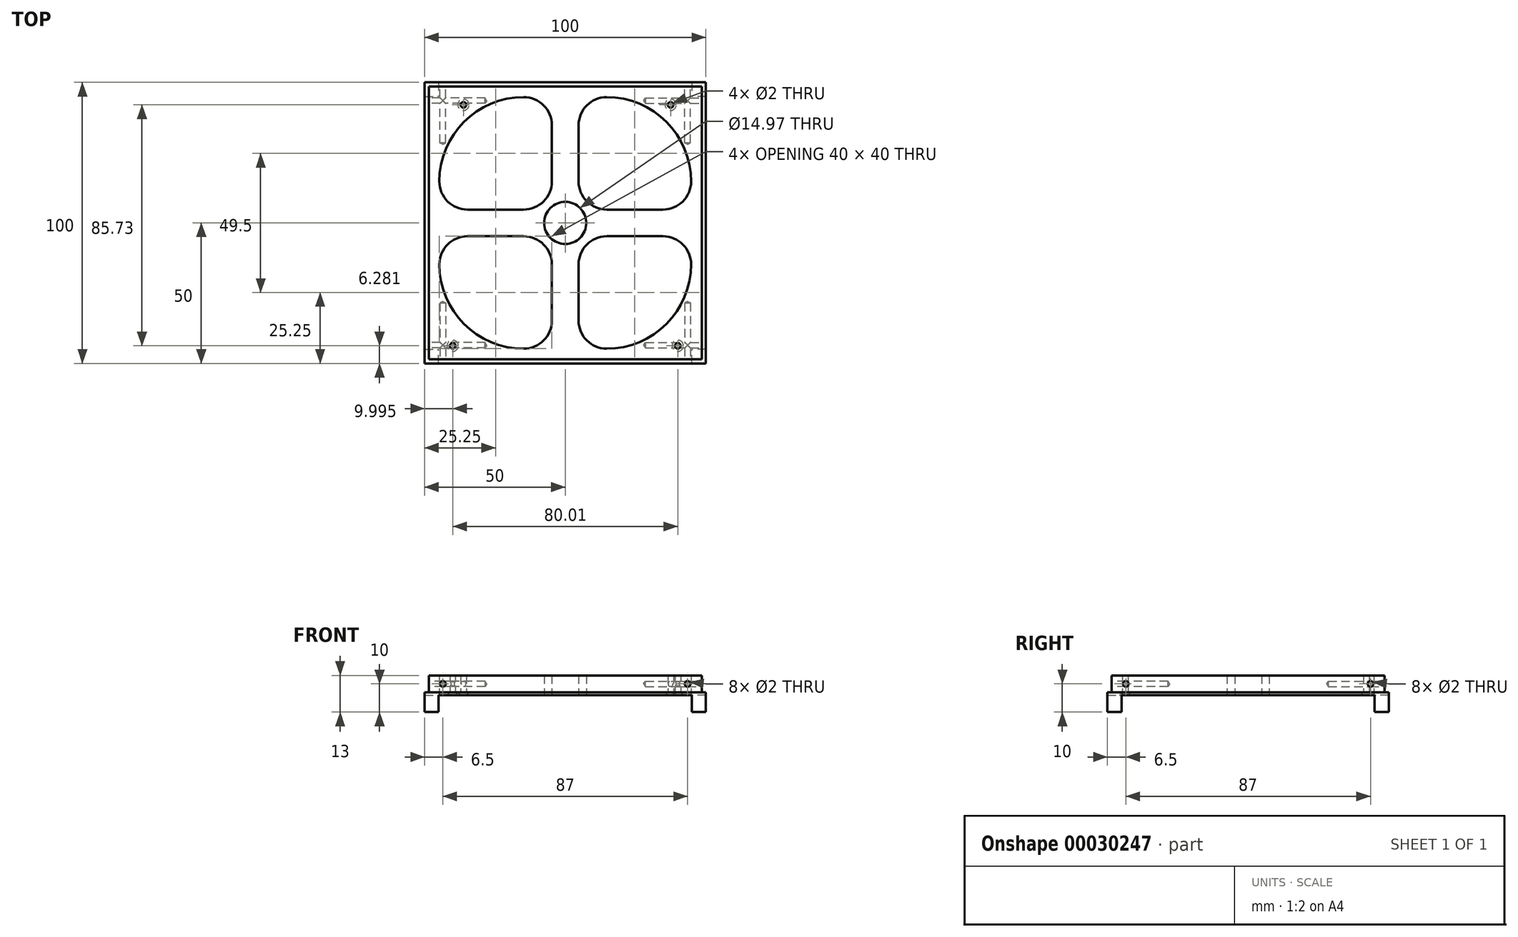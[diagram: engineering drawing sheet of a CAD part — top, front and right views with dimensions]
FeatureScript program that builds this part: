
annotation { "Feature Type Name" : "Feature", "Feature Type Description" : "" }
export const myFeature = defineFeature(function(context is Context, id is Id, definition is map)
    precondition{}
    {
        {
            var Q0;
            Q0=qCreatedBy(makeId("Top.planeOp"),FACE);
            var sketch = newSketch(context, id + "F0", { "sketchPlane" : qUnion([Q0])});
            skLineSegment(sketch, "E0.rect.bottom", {"start": v(-50, 50) * mm, "end": v(50, 50) * mm});
            skLineSegment(sketch, "E0.rect.top", {"start": v(-50, -50) * mm, "end": v(50, -50) * mm});
            skLineSegment(sketch, "E0.rect.left", {"start": v(-50, 50) * mm, "end": v(-50, -50) * mm});
            skLineSegment(sketch, "E0.rect.right", {"start": v(50, 50) * mm, "end": v(50, -50) * mm});
            skPoint(sketch, "E0.rect.middle", {"position": v(0, 0) * mm});
            skLineSegment(sketch, "E1.rect.bottom", {"start": v(-48.5, 48.5) * mm, "end": v(48.5, 48.5) * mm});
            skLineSegment(sketch, "E1.rect.top", {"start": v(-48.5, -48.5) * mm, "end": v(48.5, -48.5) * mm});
            skLineSegment(sketch, "E1.rect.left", {"start": v(-48.5, 48.5) * mm, "end": v(-48.5, -48.5) * mm});
            skLineSegment(sketch, "E1.rect.right", {"start": v(48.5, 48.5) * mm, "end": v(48.5, -48.5) * mm});
            skLineSegment(sketch, "E2.rect.bottom", {"start": v(-14.75, 4.75) * mm, "end": v(-34.75, 4.75) * mm});
            skLineSegment(sketch, "E2.rect.top", {"start": v(-14.75, 44.75) * mm, "end": v(-14.75, 44.75) * mm});
            skLineSegment(sketch, "E2.rect.left", {"start": v(-4.75, 14.75) * mm, "end": v(-4.75, 34.75) * mm});
            skLineSegment(sketch, "E2.rect.right", {"start": v(-44.75, 14.75) * mm, "end": v(-44.75, 14.75) * mm});
            skPoint(sketch, "E2.rect.middle", {"position": v(-24.75, 24.75) * mm});
            skPoint(sketch, "E3.visualSharp", {"position": v(-44.75, 44.75) * mm});
            skArc(sketch, "E3.filletArc", {"start": v(-14.75, 44.75) * mm, "mid": v(-35.96, 35.96) * mm, "end": v(-44.75, 14.75) * mm});
            skPoint(sketch, "E4.visualSharp", {"position": v(-4.75, 44.75) * mm});
            skArc(sketch, "E4.filletArc", {"start": v(-4.75, 34.75) * mm, "mid": v(-7.68, 41.82) * mm, "end": v(-14.75, 44.75) * mm});
            skPoint(sketch, "E5.visualSharp", {"position": v(-4.75, 4.75) * mm});
            skArc(sketch, "E5.filletArc", {"start": v(-14.75, 4.75) * mm, "mid": v(-7.68, 7.68) * mm, "end": v(-4.75, 14.75) * mm});
            skPoint(sketch, "E6.visualSharp", {"position": v(-44.75, 4.75) * mm});
            skArc(sketch, "E6.filletArc", {"start": v(-44.75, 14.75) * mm, "mid": v(-41.82, 7.68) * mm, "end": v(-34.75, 4.75) * mm});
            skLineSegment(sketch, "E7.MirrorCS", {"start": v(4.75, 14.75) * mm, "end": v(4.75, 34.75) * mm});
            skArc(sketch, "E8.MirrorCS", {"start": v(4.75, 34.75) * mm, "mid": v(7.68, 41.82) * mm, "end": v(14.75, 44.75) * mm});
            skLineSegment(sketch, "E9.MirrorCS", {"start": v(14.75, 44.75) * mm, "end": v(14.75, 44.75) * mm});
            skArc(sketch, "E10.MirrorCS", {"start": v(14.75, 44.75) * mm, "mid": v(35.96, 35.96) * mm, "end": v(44.75, 14.75) * mm});
            skLineSegment(sketch, "E11.MirrorCS", {"start": v(44.75, 14.75) * mm, "end": v(44.75, 14.75) * mm});
            skArc(sketch, "E12.MirrorCS", {"start": v(44.75, 14.75) * mm, "mid": v(41.82, 7.68) * mm, "end": v(34.75, 4.75) * mm});
            skLineSegment(sketch, "E13.MirrorCS", {"start": v(14.75, 4.75) * mm, "end": v(34.75, 4.75) * mm});
            skArc(sketch, "E14.MirrorCS", {"start": v(14.75, 4.75) * mm, "mid": v(7.68, 7.68) * mm, "end": v(4.75, 14.75) * mm});
            skPoint(sketch, "E15.MirrorP", {"position": v(24.75, 24.75) * mm});
            skArc(sketch, "E16.MirrorCS", {"start": v(14.75, -4.75) * mm, "mid": v(7.68, -7.68) * mm, "end": v(4.75, -14.75) * mm});
            skLineSegment(sketch, "E17.MirrorCS", {"start": v(4.75, -14.75) * mm, "end": v(4.75, -34.75) * mm});
            skArc(sketch, "E18.MirrorCS", {"start": v(4.75, -34.75) * mm, "mid": v(7.68, -41.82) * mm, "end": v(14.75, -44.75) * mm});
            skLineSegment(sketch, "E19.MirrorCS", {"start": v(14.75, -44.75) * mm, "end": v(14.75, -44.75) * mm});
            skArc(sketch, "E20.MirrorCS", {"start": v(14.75, -44.75) * mm, "mid": v(35.96, -35.96) * mm, "end": v(44.75, -14.75) * mm});
            skLineSegment(sketch, "E21.MirrorCS", {"start": v(44.75, -14.75) * mm, "end": v(44.75, -14.75) * mm});
            skArc(sketch, "E22.MirrorCS", {"start": v(44.75, -14.75) * mm, "mid": v(41.82, -7.68) * mm, "end": v(34.75, -4.75) * mm});
            skLineSegment(sketch, "E23.MirrorCS", {"start": v(14.75, -4.75) * mm, "end": v(34.75, -4.75) * mm});
            skPoint(sketch, "E24.MirrorP", {"position": v(24.75, -24.75) * mm});
            skLineSegment(sketch, "E25.MirrorCS", {"start": v(-4.75, -14.75) * mm, "end": v(-4.75, -34.75) * mm});
            skArc(sketch, "E26.MirrorCS", {"start": v(-14.75, -4.75) * mm, "mid": v(-7.68, -7.68) * mm, "end": v(-4.75, -14.75) * mm});
            skLineSegment(sketch, "E27.MirrorCS", {"start": v(-14.75, -4.75) * mm, "end": v(-34.75, -4.75) * mm});
            skArc(sketch, "E28.MirrorCS", {"start": v(-44.75, -14.75) * mm, "mid": v(-41.82, -7.68) * mm, "end": v(-34.75, -4.75) * mm});
            skLineSegment(sketch, "E29.MirrorCS", {"start": v(-44.75, -14.75) * mm, "end": v(-44.75, -14.75) * mm});
            skArc(sketch, "E30.MirrorCS", {"start": v(-14.75, -44.75) * mm, "mid": v(-35.96, -35.96) * mm, "end": v(-44.75, -14.75) * mm});
            skLineSegment(sketch, "E31.MirrorCS", {"start": v(-14.75, -44.75) * mm, "end": v(-14.75, -44.75) * mm});
            skArc(sketch, "E32.MirrorCS", {"start": v(-4.75, -34.75) * mm, "mid": v(-7.68, -41.82) * mm, "end": v(-14.75, -44.75) * mm});
            skPoint(sketch, "E33.MirrorP", {"position": v(-24.75, -24.75) * mm});
            skCircle(sketch, "E34", {"center": v(0, 0) * mm, "radius": 7.48 * mm});
            skPoint(sketch, "E35", {"position": v(-40, -42.87) * mm});
            skPoint(sketch, "E36", {"position": v(-48.5, 0) * mm});
            skPoint(sketch, "E37", {"position": v(48.5, 0) * mm});
            skLineSegment(sketch, "E38", {"start": v(-48.5, 0) * mm, "end": v(48.5, 0) * mm});
            skPoint(sketch, "E39.MirrorP", {"position": v(40, -42.87) * mm});
            skPoint(sketch, "E40", {"position": v(-36.2, 42.87) * mm});
            skPoint(sketch, "E41", {"position": v(37.47, 42.87) * mm});
            skSolve(sketch);
        }
        {
            var Q0;
            Q0=makeQuery(id+"F0.imprint","IMPRINT",FACE,{"disambiguationData":[TD([[makeQuery(id+"F0.imprint","IMPRINT",EDGE,{"derivedFrom":sQuery(id+"F0.wireOp",EDGE,"E1.rect.bottom")}),-1.0]])]});
            var Q1;
            {var subQ4=sQuery(id+"F0.wireOp",EDGE,"E1.rect.top");Q1=makeQuery(id+"F0.imprint","IMPRINT",FACE,{"disambiguationData":[TD([[makeQuery(id+"F0.imprint","IMPRINT",EDGE,{"derivedFrom":subQ4}),1.0]])]});}
            extrude(context, id + "F1", {"entities" : qUnion([Q0, Q1]), "depth" : 6 * mm});
        }
        {
            var Q0;
            Q0 = qSketchRegion(id + "F0", true);
            var Q1;
            Q1=makeQuery(id+"F1.opExtrude","CAP_FACE",FACE,{"disambiguationData":[OSD([sQuery(id+"F0.wireOp",EDGE,"E1.rect.bottom"),sQuery(id+"F0.wireOp",EDGE,"E1.rect.top"),sQuery(id+"F0.wireOp",EDGE,"E1.rect.left"),sQuery(id+"F0.wireOp",EDGE,"E1.rect.right"),sQuery(id+"F0.wireOp",EDGE,"E2.rect.bottom"),sQuery(id+"F0.wireOp",EDGE,"E2.rect.top"),sQuery(id+"F0.wireOp",EDGE,"E2.rect.left"),sQuery(id+"F0.wireOp",EDGE,"E2.rect.right"),sQuery(id+"F0.wireOp",EDGE,"d764ca65-7f6a-4e13-98eb-a7907a3d072d0.MirrorCS"),sQuery(id+"F0.wireOp",EDGE,"4e8c5bec-c53d-4312-8259-349e49f543fe0.MirrorCS"),sQuery(id+"F0.wireOp",EDGE,"d6a0bf7c-e4bc-484e-b3d5-183d898144500.MirrorCS"),sQuery(id+"F0.wireOp",EDGE,"45a758ec-378c-46c5-b086-a70cc1cacffd0.MirrorCS"),sQuery(id+"F0.wireOp",EDGE,"a64d5360-d78c-41ef-9f44-8c8436a09bba0.MirrorCS"),sQuery(id+"F0.wireOp",EDGE,"c998a958-b69a-464e-a296-dd7f6d349ec80.MirrorCS"),sQuery(id+"F0.wireOp",EDGE,"a4bf1b2a-a2f4-4ab3-9d73-85797b196d270.MirrorCS"),sQuery(id+"F0.wireOp",EDGE,"ecd2f3fb-4ea3-4913-80f4-94ebebe2d04e0.MirrorCS"),sQuery(id+"F0.wireOp",EDGE,"085a2cb5-2e3f-4cc3-a5b9-01c6e75669f10.MirrorCS"),sQuery(id+"F0.wireOp",EDGE,"73d67a52-dadc-4bd6-8141-d25047cb753b0.MirrorCS"),sQuery(id+"F0.wireOp",EDGE,"8f6832c0-858d-4205-8574-29f35786d1620.MirrorCS"),sQuery(id+"F0.wireOp",EDGE,"ecc9a695-4792-4055-9804-abf58933c5b20.MirrorCS")])],"isStart":false});
            extrude(context, id + "F2", {"entities" : qUnion([Q0, Q1]), "operationType" : NewBodyOperationType.ADD, "depth" : 1 * mm});
        }
        {
            var Q0;
            {var subQ0=sQuery(id+"F0.wireOp",EDGE,"E1.rect.bottom");Q0=makeQuery(id+"F2.boolean.opBoolean","MERGE",FACE,{"derivedFrom":[makeQuery(id+"F1.opExtrude","SWEPT_FACE",FACE,{"disambiguationData":[OSD([subQ0])]}),makeQuery(id+"F2.opExtrude","SWEPT_FACE",FACE,{"disambiguationData":[OSD([subQ0]),TDD([makeQuery(id+"F1.opExtrude","CAP_EDGE",EDGE,{"disambiguationData":[OSD([subQ0])],"isStart":false})])]})]});}
            var sketch = newSketch(context, id + "F3", { "sketchPlane" : qUnion([Q0])});
            skPoint(sketch, "E42", {"position": v(-43.5, 4) * mm});
            skPoint(sketch, "E43.MirrorP", {"position": v(43.5, 4) * mm});
            skSolve(sketch);
        }
        {
            var Q0;
            Q0=sQuery(id+"F3.wireOp",VERTEX,"E42");
            var Q1;
            Q1=sQuery(id+"F3.wireOp",VERTEX,"E43.MirrorP");
            var Q2;
            Q2=makeQuery(id+"F1.opExtrude","SWEPT_BODY",BODY,{"disambiguationData":[OSD([sQuery(id+"F0.wireOp",EDGE,"E1.rect.bottom"),sQuery(id+"F0.wireOp",EDGE,"E1.rect.top"),sQuery(id+"F0.wireOp",EDGE,"E1.rect.left"),sQuery(id+"F0.wireOp",EDGE,"E1.rect.right"),sQuery(id+"F0.wireOp",EDGE,"E2.rect.bottom"),sQuery(id+"F0.wireOp",EDGE,"E2.rect.top"),sQuery(id+"F0.wireOp",EDGE,"E2.rect.left"),sQuery(id+"F0.wireOp",EDGE,"E2.rect.right"),sQuery(id+"F0.wireOp",EDGE,"E3.filletArc"),sQuery(id+"F0.wireOp",EDGE,"E4.filletArc"),sQuery(id+"F0.wireOp",EDGE,"E5.filletArc"),sQuery(id+"F0.wireOp",EDGE,"E6.filletArc"),sQuery(id+"F0.wireOp",EDGE,"E7.MirrorCS"),sQuery(id+"F0.wireOp",EDGE,"E8.MirrorCS"),sQuery(id+"F0.wireOp",EDGE,"E9.MirrorCS"),sQuery(id+"F0.wireOp",EDGE,"E10.MirrorCS"),sQuery(id+"F0.wireOp",EDGE,"E11.MirrorCS"),sQuery(id+"F0.wireOp",EDGE,"E12.MirrorCS"),sQuery(id+"F0.wireOp",EDGE,"E13.MirrorCS"),sQuery(id+"F0.wireOp",EDGE,"E14.MirrorCS"),sQuery(id+"F0.wireOp",EDGE,"E16.MirrorCS"),sQuery(id+"F0.wireOp",EDGE,"E17.MirrorCS"),sQuery(id+"F0.wireOp",EDGE,"E18.MirrorCS"),sQuery(id+"F0.wireOp",EDGE,"E19.MirrorCS"),sQuery(id+"F0.wireOp",EDGE,"E20.MirrorCS"),sQuery(id+"F0.wireOp",EDGE,"E21.MirrorCS"),sQuery(id+"F0.wireOp",EDGE,"E22.MirrorCS"),sQuery(id+"F0.wireOp",EDGE,"E23.MirrorCS"),sQuery(id+"F0.wireOp",EDGE,"E25.MirrorCS"),sQuery(id+"F0.wireOp",EDGE,"E26.MirrorCS"),sQuery(id+"F0.wireOp",EDGE,"E27.MirrorCS"),sQuery(id+"F0.wireOp",EDGE,"E28.MirrorCS"),sQuery(id+"F0.wireOp",EDGE,"E29.MirrorCS"),sQuery(id+"F0.wireOp",EDGE,"E30.MirrorCS"),sQuery(id+"F0.wireOp",EDGE,"E31.MirrorCS"),sQuery(id+"F0.wireOp",EDGE,"E32.MirrorCS")])]});
            hole(context, id + "F4", {"style" : HoleStyle.SIMPLE, "holeDiameter" : 2 * mm, "endStyle" : HoleEndStyle.BLIND, "holeDepth" : 20 * mm, "locations" : qUnion([Q0, Q1]), "scope" : qUnion([Q2])});
        }
        {
            var Q0;
            {var subQ0=sQuery(id+"F0.wireOp",EDGE,"E1.rect.left");Q0=makeQuery(id+"F2.boolean.opBoolean","MERGE",FACE,{"derivedFrom":[makeQuery(id+"F1.opExtrude","SWEPT_FACE",FACE,{"disambiguationData":[OSD([subQ0])]}),makeQuery(id+"F2.opExtrude","SWEPT_FACE",FACE,{"disambiguationData":[OSD([subQ0]),TDD([makeQuery(id+"F1.opExtrude","CAP_EDGE",EDGE,{"disambiguationData":[OSD([subQ0])],"isStart":false})])]})]});}
            var sketch = newSketch(context, id + "F5", { "sketchPlane" : qUnion([Q0])});
            skPoint(sketch, "E44", {"position": v(-43.5, 4) * mm});
            skPoint(sketch, "E45.MirrorP", {"position": v(43.5, 4) * mm});
            skSolve(sketch);
        }
        {
            var Q0;
            Q0=sQuery(id+"F5.wireOp",VERTEX,"E44");
            var Q1;
            Q1=sQuery(id+"F5.wireOp",VERTEX,"E45.MirrorP");
            var Q2;
            Q2=makeQuery(id+"F1.opExtrude","SWEPT_BODY",BODY,{"disambiguationData":[OSD([sQuery(id+"F0.wireOp",EDGE,"E1.rect.bottom"),sQuery(id+"F0.wireOp",EDGE,"E1.rect.top"),sQuery(id+"F0.wireOp",EDGE,"E1.rect.left"),sQuery(id+"F0.wireOp",EDGE,"E1.rect.right"),sQuery(id+"F0.wireOp",EDGE,"E2.rect.bottom"),sQuery(id+"F0.wireOp",EDGE,"E2.rect.top"),sQuery(id+"F0.wireOp",EDGE,"E2.rect.left"),sQuery(id+"F0.wireOp",EDGE,"E2.rect.right"),sQuery(id+"F0.wireOp",EDGE,"E3.filletArc"),sQuery(id+"F0.wireOp",EDGE,"E4.filletArc"),sQuery(id+"F0.wireOp",EDGE,"E5.filletArc"),sQuery(id+"F0.wireOp",EDGE,"E6.filletArc"),sQuery(id+"F0.wireOp",EDGE,"E7.MirrorCS"),sQuery(id+"F0.wireOp",EDGE,"E8.MirrorCS"),sQuery(id+"F0.wireOp",EDGE,"E9.MirrorCS"),sQuery(id+"F0.wireOp",EDGE,"E10.MirrorCS"),sQuery(id+"F0.wireOp",EDGE,"E11.MirrorCS"),sQuery(id+"F0.wireOp",EDGE,"E12.MirrorCS"),sQuery(id+"F0.wireOp",EDGE,"E13.MirrorCS"),sQuery(id+"F0.wireOp",EDGE,"E14.MirrorCS"),sQuery(id+"F0.wireOp",EDGE,"E16.MirrorCS"),sQuery(id+"F0.wireOp",EDGE,"E17.MirrorCS"),sQuery(id+"F0.wireOp",EDGE,"E18.MirrorCS"),sQuery(id+"F0.wireOp",EDGE,"E19.MirrorCS"),sQuery(id+"F0.wireOp",EDGE,"E20.MirrorCS"),sQuery(id+"F0.wireOp",EDGE,"E21.MirrorCS"),sQuery(id+"F0.wireOp",EDGE,"E22.MirrorCS"),sQuery(id+"F0.wireOp",EDGE,"E23.MirrorCS"),sQuery(id+"F0.wireOp",EDGE,"E25.MirrorCS"),sQuery(id+"F0.wireOp",EDGE,"E26.MirrorCS"),sQuery(id+"F0.wireOp",EDGE,"E27.MirrorCS"),sQuery(id+"F0.wireOp",EDGE,"E28.MirrorCS"),sQuery(id+"F0.wireOp",EDGE,"E29.MirrorCS"),sQuery(id+"F0.wireOp",EDGE,"E30.MirrorCS"),sQuery(id+"F0.wireOp",EDGE,"E31.MirrorCS"),sQuery(id+"F0.wireOp",EDGE,"E32.MirrorCS")])]});
            hole(context, id + "F6", {"style" : HoleStyle.SIMPLE, "holeDiameter" : 2 * mm, "endStyle" : HoleEndStyle.BLIND, "holeDepth" : 20 * mm, "locations" : qUnion([Q0, Q1]), "scope" : qUnion([Q2])});
        }
        {
            var Q0;
            {var subQ0=sQuery(id+"F0.wireOp",EDGE,"E1.rect.top");Q0=makeQuery(id+"F2.boolean.opBoolean","MERGE",FACE,{"derivedFrom":[makeQuery(id+"F1.opExtrude","SWEPT_FACE",FACE,{"disambiguationData":[OSD([subQ0])]}),makeQuery(id+"F2.opExtrude","SWEPT_FACE",FACE,{"disambiguationData":[OSD([subQ0]),TDD([makeQuery(id+"F1.opExtrude","CAP_EDGE",EDGE,{"disambiguationData":[OSD([subQ0])],"isStart":false})])]})]});}
            var sketch = newSketch(context, id + "F7", { "sketchPlane" : qUnion([Q0])});
            skPoint(sketch, "E46", {"position": v(-43.5, 4) * mm});
            skPoint(sketch, "E47.MirrorP", {"position": v(43.5, 4) * mm});
            skSolve(sketch);
        }
        {
            var Q0;
            Q0=sQuery(id+"F7.wireOp",VERTEX,"E46");
            var Q1;
            Q1=sQuery(id+"F7.wireOp",VERTEX,"E47.MirrorP");
            var Q2;
            Q2=makeQuery(id+"F1.opExtrude","SWEPT_BODY",BODY,{"disambiguationData":[OSD([sQuery(id+"F0.wireOp",EDGE,"E1.rect.bottom"),sQuery(id+"F0.wireOp",EDGE,"E1.rect.top"),sQuery(id+"F0.wireOp",EDGE,"E1.rect.left"),sQuery(id+"F0.wireOp",EDGE,"E1.rect.right"),sQuery(id+"F0.wireOp",EDGE,"E2.rect.bottom"),sQuery(id+"F0.wireOp",EDGE,"E2.rect.top"),sQuery(id+"F0.wireOp",EDGE,"E2.rect.left"),sQuery(id+"F0.wireOp",EDGE,"E2.rect.right"),sQuery(id+"F0.wireOp",EDGE,"E3.filletArc"),sQuery(id+"F0.wireOp",EDGE,"E4.filletArc"),sQuery(id+"F0.wireOp",EDGE,"E5.filletArc"),sQuery(id+"F0.wireOp",EDGE,"E6.filletArc"),sQuery(id+"F0.wireOp",EDGE,"E7.MirrorCS"),sQuery(id+"F0.wireOp",EDGE,"E8.MirrorCS"),sQuery(id+"F0.wireOp",EDGE,"E9.MirrorCS"),sQuery(id+"F0.wireOp",EDGE,"E10.MirrorCS"),sQuery(id+"F0.wireOp",EDGE,"E11.MirrorCS"),sQuery(id+"F0.wireOp",EDGE,"E12.MirrorCS"),sQuery(id+"F0.wireOp",EDGE,"E13.MirrorCS"),sQuery(id+"F0.wireOp",EDGE,"E14.MirrorCS"),sQuery(id+"F0.wireOp",EDGE,"E16.MirrorCS"),sQuery(id+"F0.wireOp",EDGE,"E17.MirrorCS"),sQuery(id+"F0.wireOp",EDGE,"E18.MirrorCS"),sQuery(id+"F0.wireOp",EDGE,"E19.MirrorCS"),sQuery(id+"F0.wireOp",EDGE,"E20.MirrorCS"),sQuery(id+"F0.wireOp",EDGE,"E21.MirrorCS"),sQuery(id+"F0.wireOp",EDGE,"E22.MirrorCS"),sQuery(id+"F0.wireOp",EDGE,"E23.MirrorCS"),sQuery(id+"F0.wireOp",EDGE,"E25.MirrorCS"),sQuery(id+"F0.wireOp",EDGE,"E26.MirrorCS"),sQuery(id+"F0.wireOp",EDGE,"E27.MirrorCS"),sQuery(id+"F0.wireOp",EDGE,"E28.MirrorCS"),sQuery(id+"F0.wireOp",EDGE,"E29.MirrorCS"),sQuery(id+"F0.wireOp",EDGE,"E30.MirrorCS"),sQuery(id+"F0.wireOp",EDGE,"E31.MirrorCS"),sQuery(id+"F0.wireOp",EDGE,"E32.MirrorCS")])]});
            hole(context, id + "F8", {"style" : HoleStyle.SIMPLE, "holeDiameter" : 2 * mm, "endStyle" : HoleEndStyle.BLIND, "holeDepth" : 20 * mm, "locations" : qUnion([Q0, Q1]), "scope" : qUnion([Q2])});
        }
        {
            var Q0;
            {var subQ0=sQuery(id+"F0.wireOp",EDGE,"E1.rect.right");Q0=makeQuery(id+"F2.boolean.opBoolean","MERGE",FACE,{"derivedFrom":[makeQuery(id+"F1.opExtrude","SWEPT_FACE",FACE,{"disambiguationData":[OSD([subQ0])]}),makeQuery(id+"F2.opExtrude","SWEPT_FACE",FACE,{"disambiguationData":[OSD([subQ0]),TDD([makeQuery(id+"F1.opExtrude","CAP_EDGE",EDGE,{"disambiguationData":[OSD([subQ0])],"isStart":false})])]})]});}
            var sketch = newSketch(context, id + "F9", { "sketchPlane" : qUnion([Q0])});
            skPoint(sketch, "E48", {"position": v(-43.5, 4) * mm});
            skPoint(sketch, "E49.MirrorP", {"position": v(43.5, 4) * mm});
            skSolve(sketch);
        }
        {
            var Q0;
            Q0=sQuery(id+"F9.wireOp",VERTEX,"E48");
            var Q1;
            Q1=sQuery(id+"F9.wireOp",VERTEX,"E49.MirrorP");
            var Q2;
            Q2=makeQuery(id+"F1.opExtrude","SWEPT_BODY",BODY,{"disambiguationData":[OSD([sQuery(id+"F0.wireOp",EDGE,"E1.rect.bottom"),sQuery(id+"F0.wireOp",EDGE,"E1.rect.top"),sQuery(id+"F0.wireOp",EDGE,"E1.rect.left"),sQuery(id+"F0.wireOp",EDGE,"E1.rect.right"),sQuery(id+"F0.wireOp",EDGE,"E2.rect.bottom"),sQuery(id+"F0.wireOp",EDGE,"E2.rect.top"),sQuery(id+"F0.wireOp",EDGE,"E2.rect.left"),sQuery(id+"F0.wireOp",EDGE,"E2.rect.right"),sQuery(id+"F0.wireOp",EDGE,"E3.filletArc"),sQuery(id+"F0.wireOp",EDGE,"E4.filletArc"),sQuery(id+"F0.wireOp",EDGE,"E5.filletArc"),sQuery(id+"F0.wireOp",EDGE,"E6.filletArc"),sQuery(id+"F0.wireOp",EDGE,"E7.MirrorCS"),sQuery(id+"F0.wireOp",EDGE,"E8.MirrorCS"),sQuery(id+"F0.wireOp",EDGE,"E9.MirrorCS"),sQuery(id+"F0.wireOp",EDGE,"E10.MirrorCS"),sQuery(id+"F0.wireOp",EDGE,"E11.MirrorCS"),sQuery(id+"F0.wireOp",EDGE,"E12.MirrorCS"),sQuery(id+"F0.wireOp",EDGE,"E13.MirrorCS"),sQuery(id+"F0.wireOp",EDGE,"E14.MirrorCS"),sQuery(id+"F0.wireOp",EDGE,"E16.MirrorCS"),sQuery(id+"F0.wireOp",EDGE,"E17.MirrorCS"),sQuery(id+"F0.wireOp",EDGE,"E18.MirrorCS"),sQuery(id+"F0.wireOp",EDGE,"E19.MirrorCS"),sQuery(id+"F0.wireOp",EDGE,"E20.MirrorCS"),sQuery(id+"F0.wireOp",EDGE,"E21.MirrorCS"),sQuery(id+"F0.wireOp",EDGE,"E22.MirrorCS"),sQuery(id+"F0.wireOp",EDGE,"E23.MirrorCS"),sQuery(id+"F0.wireOp",EDGE,"E25.MirrorCS"),sQuery(id+"F0.wireOp",EDGE,"E26.MirrorCS"),sQuery(id+"F0.wireOp",EDGE,"E27.MirrorCS"),sQuery(id+"F0.wireOp",EDGE,"E28.MirrorCS"),sQuery(id+"F0.wireOp",EDGE,"E29.MirrorCS"),sQuery(id+"F0.wireOp",EDGE,"E30.MirrorCS"),sQuery(id+"F0.wireOp",EDGE,"E31.MirrorCS"),sQuery(id+"F0.wireOp",EDGE,"E32.MirrorCS")])]});
            hole(context, id + "F10", {"style" : HoleStyle.SIMPLE, "holeDiameter" : 2 * mm, "endStyle" : HoleEndStyle.BLIND, "holeDepth" : 20 * mm, "locations" : qUnion([Q0, Q1]), "scope" : qUnion([Q2])});
        }
        {
            var Q0;
            {var subQ0=sQuery(id+"F0.wireOp",EDGE,"E1.rect.bottom");var subQ1=sQuery(id+"F0.wireOp",EDGE,"E1.rect.top");var subQ2=sQuery(id+"F0.wireOp",EDGE,"E1.rect.left");var subQ3=sQuery(id+"F0.wireOp",EDGE,"E1.rect.right");Q0=makeQuery(id+"F2.boolean.opBoolean","MERGE",FACE,{"derivedFrom":[makeQuery(id+"F1.opExtrude","CAP_FACE",FACE,{"disambiguationData":[OSD([subQ0,subQ1,subQ2,subQ3,sQuery(id+"F0.wireOp",EDGE,"E2.rect.bottom"),sQuery(id+"F0.wireOp",EDGE,"E2.rect.top"),sQuery(id+"F0.wireOp",EDGE,"E2.rect.left"),sQuery(id+"F0.wireOp",EDGE,"E2.rect.right"),sQuery(id+"F0.wireOp",EDGE,"E3.filletArc"),sQuery(id+"F0.wireOp",EDGE,"E4.filletArc"),sQuery(id+"F0.wireOp",EDGE,"E5.filletArc"),sQuery(id+"F0.wireOp",EDGE,"E6.filletArc"),sQuery(id+"F0.wireOp",EDGE,"E7.MirrorCS"),sQuery(id+"F0.wireOp",EDGE,"E8.MirrorCS"),sQuery(id+"F0.wireOp",EDGE,"E9.MirrorCS"),sQuery(id+"F0.wireOp",EDGE,"E10.MirrorCS"),sQuery(id+"F0.wireOp",EDGE,"E11.MirrorCS"),sQuery(id+"F0.wireOp",EDGE,"E12.MirrorCS"),sQuery(id+"F0.wireOp",EDGE,"E13.MirrorCS"),sQuery(id+"F0.wireOp",EDGE,"E14.MirrorCS"),sQuery(id+"F0.wireOp",EDGE,"E16.MirrorCS"),sQuery(id+"F0.wireOp",EDGE,"E17.MirrorCS"),sQuery(id+"F0.wireOp",EDGE,"E18.MirrorCS"),sQuery(id+"F0.wireOp",EDGE,"E19.MirrorCS"),sQuery(id+"F0.wireOp",EDGE,"E20.MirrorCS"),sQuery(id+"F0.wireOp",EDGE,"E21.MirrorCS"),sQuery(id+"F0.wireOp",EDGE,"E22.MirrorCS"),sQuery(id+"F0.wireOp",EDGE,"E23.MirrorCS"),sQuery(id+"F0.wireOp",EDGE,"E25.MirrorCS"),sQuery(id+"F0.wireOp",EDGE,"E26.MirrorCS"),sQuery(id+"F0.wireOp",EDGE,"E27.MirrorCS"),sQuery(id+"F0.wireOp",EDGE,"E28.MirrorCS"),sQuery(id+"F0.wireOp",EDGE,"E29.MirrorCS"),sQuery(id+"F0.wireOp",EDGE,"E30.MirrorCS"),sQuery(id+"F0.wireOp",EDGE,"E31.MirrorCS"),sQuery(id+"F0.wireOp",EDGE,"E32.MirrorCS")])],"isStart":true}),makeQuery(id+"F2.opExtrude","CAP_FACE",FACE,{"disambiguationData":[OSD([sQuery(id+"F0.wireOp",EDGE,"E0.rect.bottom"),sQuery(id+"F0.wireOp",EDGE,"E0.rect.top"),sQuery(id+"F0.wireOp",EDGE,"E0.rect.left"),sQuery(id+"F0.wireOp",EDGE,"E0.rect.right"),subQ0,subQ1,subQ2,subQ3])],"isStart":true})]});}
            var sketch = newSketch(context, id + "F11", { "sketchPlane" : qUnion([Q0])});
            skPoint(sketch, "E50", {"position": v(-36.2, -42.01) * mm});
            skPoint(sketch, "E51", {"position": v(40, 43.72) * mm});
            skPoint(sketch, "E52", {"position": v(37.47, -42.01) * mm});
            skPoint(sketch, "E53", {"position": v(-40, 43.72) * mm});
            skLineSegment(sketch, "E54.bottom", {"start": v(50, -50) * mm, "end": v(45, -50) * mm});
            skLineSegment(sketch, "E54.top", {"start": v(50, -45) * mm, "end": v(45, -45) * mm});
            skLineSegment(sketch, "E54.left", {"start": v(50, -50) * mm, "end": v(50, -45) * mm});
            skLineSegment(sketch, "E54.right", {"start": v(45, -50) * mm, "end": v(45, -45) * mm});
            skLineSegment(sketch, "E55.MirrorCS", {"start": v(-50, -50) * mm, "end": v(-50, -45) * mm});
            skLineSegment(sketch, "E56.MirrorCS", {"start": v(-45, -50) * mm, "end": v(-45, -45) * mm});
            skLineSegment(sketch, "E57.MirrorCS", {"start": v(-50, -45) * mm, "end": v(-45, -45) * mm});
            skLineSegment(sketch, "E58.MirrorCS", {"start": v(-50, -50) * mm, "end": v(-45, -50) * mm});
            skLineSegment(sketch, "E59.MirrorCS", {"start": v(-50, 50) * mm, "end": v(-45, 50) * mm});
            skLineSegment(sketch, "E60.MirrorCS", {"start": v(-50, 45) * mm, "end": v(-45, 45) * mm});
            skLineSegment(sketch, "E61.MirrorCS", {"start": v(-50, 50) * mm, "end": v(-50, 45) * mm});
            skLineSegment(sketch, "E62.MirrorCS", {"start": v(-45, 50) * mm, "end": v(-45, 45) * mm});
            skLineSegment(sketch, "E63.MirrorCS", {"start": v(50, 50) * mm, "end": v(45, 50) * mm});
            skLineSegment(sketch, "E64.MirrorCS", {"start": v(50, 45) * mm, "end": v(45, 45) * mm});
            skLineSegment(sketch, "E65.MirrorCS", {"start": v(50, 50) * mm, "end": v(50, 45) * mm});
            skLineSegment(sketch, "E66.MirrorCS", {"start": v(45, 50) * mm, "end": v(45, 45) * mm});
            skSolve(sketch);
        }
        {
            var Q0;
            Q0=sQuery(id+"F11.wireOp",VERTEX,"E50");
            var Q1;
            Q1=sQuery(id+"F11.wireOp",VERTEX,"E53");
            var Q2;
            Q2=sQuery(id+"F11.wireOp",VERTEX,"E51");
            var Q3;
            Q3=sQuery(id+"F11.wireOp",VERTEX,"E52");
            var Q4;
            Q4=makeQuery(id+"F1.opExtrude","SWEPT_BODY",BODY,{"disambiguationData":[OSD([sQuery(id+"F0.wireOp",EDGE,"E1.rect.bottom"),sQuery(id+"F0.wireOp",EDGE,"E1.rect.top"),sQuery(id+"F0.wireOp",EDGE,"E1.rect.left"),sQuery(id+"F0.wireOp",EDGE,"E1.rect.right"),sQuery(id+"F0.wireOp",EDGE,"E2.rect.bottom"),sQuery(id+"F0.wireOp",EDGE,"E2.rect.top"),sQuery(id+"F0.wireOp",EDGE,"E2.rect.left"),sQuery(id+"F0.wireOp",EDGE,"E2.rect.right"),sQuery(id+"F0.wireOp",EDGE,"E3.filletArc"),sQuery(id+"F0.wireOp",EDGE,"E4.filletArc"),sQuery(id+"F0.wireOp",EDGE,"E5.filletArc"),sQuery(id+"F0.wireOp",EDGE,"E6.filletArc"),sQuery(id+"F0.wireOp",EDGE,"E7.MirrorCS"),sQuery(id+"F0.wireOp",EDGE,"E8.MirrorCS"),sQuery(id+"F0.wireOp",EDGE,"E9.MirrorCS"),sQuery(id+"F0.wireOp",EDGE,"E10.MirrorCS"),sQuery(id+"F0.wireOp",EDGE,"E11.MirrorCS"),sQuery(id+"F0.wireOp",EDGE,"E12.MirrorCS"),sQuery(id+"F0.wireOp",EDGE,"E13.MirrorCS"),sQuery(id+"F0.wireOp",EDGE,"E14.MirrorCS"),sQuery(id+"F0.wireOp",EDGE,"E16.MirrorCS"),sQuery(id+"F0.wireOp",EDGE,"E17.MirrorCS"),sQuery(id+"F0.wireOp",EDGE,"E18.MirrorCS"),sQuery(id+"F0.wireOp",EDGE,"E19.MirrorCS"),sQuery(id+"F0.wireOp",EDGE,"E20.MirrorCS"),sQuery(id+"F0.wireOp",EDGE,"E21.MirrorCS"),sQuery(id+"F0.wireOp",EDGE,"E22.MirrorCS"),sQuery(id+"F0.wireOp",EDGE,"E23.MirrorCS"),sQuery(id+"F0.wireOp",EDGE,"E25.MirrorCS"),sQuery(id+"F0.wireOp",EDGE,"E26.MirrorCS"),sQuery(id+"F0.wireOp",EDGE,"E27.MirrorCS"),sQuery(id+"F0.wireOp",EDGE,"E28.MirrorCS"),sQuery(id+"F0.wireOp",EDGE,"E29.MirrorCS"),sQuery(id+"F0.wireOp",EDGE,"E30.MirrorCS"),sQuery(id+"F0.wireOp",EDGE,"E31.MirrorCS"),sQuery(id+"F0.wireOp",EDGE,"E32.MirrorCS")])]});
            hole(context, id + "F12", {"style" : HoleStyle.C_SINK, "holeDiameter" : 2 * mm, "cSinkDiameter" : 4 * mm, "endStyle" : HoleEndStyle.THROUGH, "locations" : qUnion([Q0, Q1, Q2, Q3]), "scope" : qUnion([Q4]), "cSinkAngle" : 90 * degree});
        }
        {
            var Q0;
            Q0=makeQuery(id+"F11.imprint","IMPRINT",FACE,{"disambiguationData":[TD([[makeQuery(id+"F11.imprint","IMPRINT",EDGE,{"derivedFrom":sQuery(id+"F11.wireOp",EDGE,"E59.MirrorCS")}),-1.0]])]});
            var Q1;
            Q1=makeQuery(id+"F11.imprint","IMPRINT",FACE,{"disambiguationData":[TD([[makeQuery(id+"F11.imprint","IMPRINT",EDGE,{"derivedFrom":sQuery(id+"F11.wireOp",EDGE,"E63.MirrorCS")}),-1.0]])]});
            var Q2;
            Q2=makeQuery(id+"F11.imprint","IMPRINT",FACE,{"disambiguationData":[TD([[makeQuery(id+"F11.imprint","IMPRINT",EDGE,{"derivedFrom":sQuery(id+"F11.wireOp",EDGE,"E54.bottom")}),1.0]])]});
            var Q3;
            Q3=makeQuery(id+"F11.imprint","IMPRINT",FACE,{"disambiguationData":[TD([[makeQuery(id+"F11.imprint","IMPRINT",EDGE,{"derivedFrom":sQuery(id+"F11.wireOp",EDGE,"E55.MirrorCS")}),-1.0]])]});
            extrude(context, id + "F13", {"entities" : qUnion([Q0, Q1, Q2, Q3]), "operationType" : NewBodyOperationType.ADD, "depth" : 6 * mm});
        }
    });
